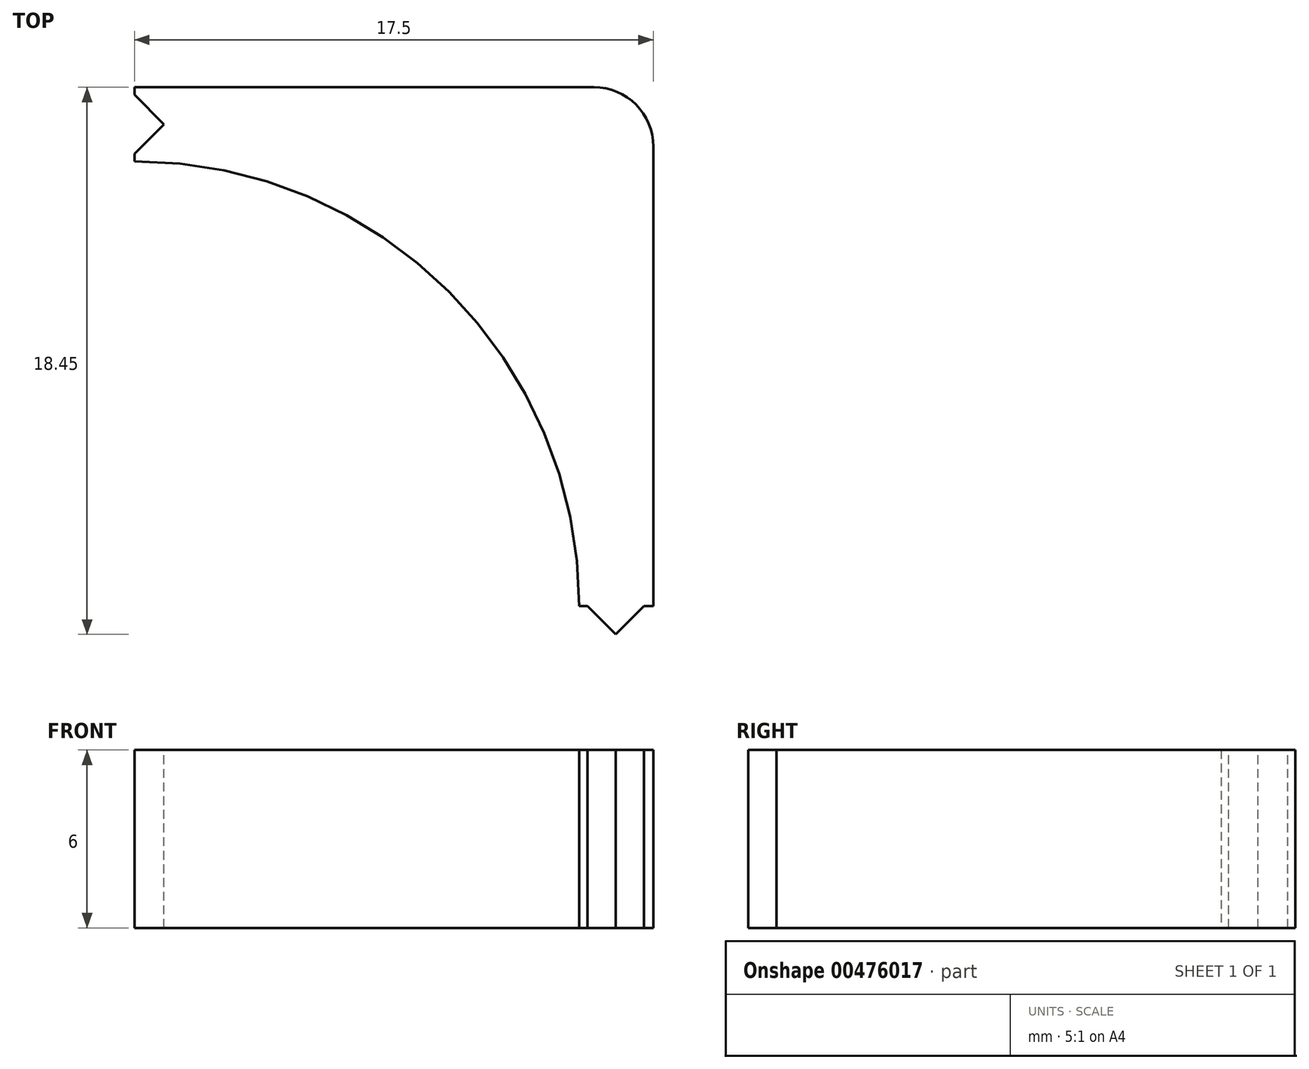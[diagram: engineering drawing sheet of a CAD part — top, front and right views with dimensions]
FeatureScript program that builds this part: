
annotation { "Feature Type Name" : "Feature", "Feature Type Description" : "" }
export const myFeature = defineFeature(function(context is Context, id is Id, definition is map)
    precondition{}
    {
        {
            var Q0;
            Q0=qCreatedBy(makeId("Top.planeOp"),FACE);
            var sketch = newSketch(context, id + "F0", { "sketchPlane" : qUnion([Q0])});
            skLineSegment(sketch, "E0.bottom", {"start": v(-15.5, 17.5) * mm, "end": v(15.5, 17.5) * mm});
            skLineSegment(sketch, "E0.top", {"start": v(-15.5, -17.5) * mm, "end": v(15.5, -17.5) * mm});
            skLineSegment(sketch, "E0.left", {"start": v(-17.5, 15.5) * mm, "end": v(-17.5, -15.5) * mm});
            skLineSegment(sketch, "E0.right", {"start": v(17.5, 15.5) * mm, "end": v(17.5, -15.5) * mm});
            skPoint(sketch, "E0.middle", {"position": v(0, 0) * mm});
            skCircle(sketch, "E1", {"center": v(0, 0) * mm, "radius": 15 * mm});
            skPoint(sketch, "E2.visualSharp", {"position": v(-17.5, 17.5) * mm});
            skArc(sketch, "E2.filletArc", {"start": v(-15.5, 17.5) * mm, "mid": v(-16.91, 16.91) * mm, "end": v(-17.5, 15.5) * mm});
            skPoint(sketch, "E3.visualSharp", {"position": v(17.5, 17.5) * mm});
            skArc(sketch, "E3.filletArc", {"start": v(17.5, 15.5) * mm, "mid": v(16.91, 16.91) * mm, "end": v(15.5, 17.5) * mm});
            skPoint(sketch, "E4.visualSharp", {"position": v(17.5, -17.5) * mm});
            skArc(sketch, "E4.filletArc", {"start": v(15.5, -17.5) * mm, "mid": v(16.91, -16.91) * mm, "end": v(17.5, -15.5) * mm});
            skPoint(sketch, "E5.visualSharp", {"position": v(-17.5, -17.5) * mm});
            skArc(sketch, "E5.filletArc", {"start": v(-17.5, -15.5) * mm, "mid": v(-16.91, -16.91) * mm, "end": v(-15.5, -17.5) * mm});
            skSolve(sketch);
        }
        {
            var Q0;
            Q0 = qSketchRegion(id + "F0", true);
            extrude(context, id + "F1", {"entities" : qUnion([Q0]), "depth" : 6 * mm});
        }
        {
            var Q0;
            Q0=makeQuery(id+"F1.opExtrude","CAP_FACE",FACE,{"disambiguationData":[OSD([sQuery(id+"F0.wireOp",EDGE,"E0.bottom"),sQuery(id+"F0.wireOp",EDGE,"E0.top"),sQuery(id+"F0.wireOp",EDGE,"E0.left"),sQuery(id+"F0.wireOp",EDGE,"E0.right"),sQuery(id+"F0.wireOp",EDGE,"E1"),sQuery(id+"F0.wireOp",EDGE,"E2.filletArc"),sQuery(id+"F0.wireOp",EDGE,"E3.filletArc"),sQuery(id+"F0.wireOp",EDGE,"E4.filletArc"),sQuery(id+"F0.wireOp",EDGE,"E5.filletArc")])],"isStart":false});
            var sketch = newSketch(context, id + "F2", { "sketchPlane" : qUnion([Q0])});
            skLineSegment(sketch, "E6", {"start": v(0, 17.5) * mm, "end": v(0, 0) * mm});
            skLineSegment(sketch, "E7", {"start": v(0, 0) * mm, "end": v(17.5, 0) * mm});
            skLineSegment(sketch, "E8", {"start": v(17.5, 0) * mm, "end": v(17.5, -17.5) * mm});
            skPoint(sketch, "E9.endSnap0", {"position": v(-16.91, -16.91) * mm});
            skLineSegment(sketch, "E10", {"start": v(17.5, -17.5) * mm, "end": v(-17.5, -17.5) * mm});
            skLineSegment(sketch, "E11", {"start": v(-17.5, -17.5) * mm, "end": v(-17.5, 17.5) * mm});
            skLineSegment(sketch, "E12", {"start": v(-17.5, 17.5) * mm, "end": v(0, 17.5) * mm});
            skSolve(sketch);
        }
        {
            var Q0;
            Q0 = qSketchRegion(id + "F2", true);
            extrude(context, id + "F3", {"entities" : qUnion([Q0]), "operationType" : NewBodyOperationType.REMOVE, "oppositeDirection" : true, "depth" : 25 * mm});
        }
        {
            var Q0;
            Q0=makeQuery(id+"F1.opExtrude","CAP_FACE",FACE,{"disambiguationData":[OSD([sQuery(id+"F0.wireOp",EDGE,"E0.bottom"),sQuery(id+"F0.wireOp",EDGE,"E0.top"),sQuery(id+"F0.wireOp",EDGE,"E0.left"),sQuery(id+"F0.wireOp",EDGE,"E0.right"),sQuery(id+"F0.wireOp",EDGE,"E1"),sQuery(id+"F0.wireOp",EDGE,"E2.filletArc"),sQuery(id+"F0.wireOp",EDGE,"E3.filletArc"),sQuery(id+"F0.wireOp",EDGE,"E4.filletArc"),sQuery(id+"F0.wireOp",EDGE,"E5.filletArc")])],"isStart":false});
            var sketch = newSketch(context, id + "F4", { "sketchPlane" : qUnion([Q0])});
            skLineSegment(sketch, "E13", {"start": v(16.25, 0) * mm, "end": v(16.25, -1) * mm, "construction": true});
            skSolve(sketch);
        }
        {
            var Q0;
            Q0=makeQuery(id+"F4.imprint","IMPRINT",FACE,{"disambiguationData":[TD([[makeQuery(id+"F4.imprint","IMPRINT",EDGE,{"derivedFrom":makeQuery(id+"F1.opExtrude","CAP_EDGE",EDGE,{"disambiguationData":[OSD([sQuery(id+"F0.wireOp",EDGE,"E3.filletArc")])],"isStart":false})}),1.0]])]});
            var sketch = newSketch(context, id + "F5", { "sketchPlane" : qUnion([Q0])});
            skLineSegment(sketch, "E14", {"start": v(16.23, -0.95) * mm, "end": v(17.18, 0) * mm});
            skLineSegment(sketch, "E15", {"start": v(17.18, 0) * mm, "end": v(15.28, 0) * mm});
            skLineSegment(sketch, "E16", {"start": v(15.28, 0) * mm, "end": v(16.23, -0.95) * mm});
            skSolve(sketch);
        }
        {
            var Q0;
            Q0 = qSketchRegion(id + "F5", true);
            extrude(context, id + "F6", {"entities" : qUnion([Q0]), "operationType" : NewBodyOperationType.ADD, "oppositeDirection" : true, "depth" : 6 * mm});
        }
        {
            var Q0;
            Q0=makeQuery(id+"F4.imprint","IMPRINT",FACE,{"disambiguationData":[TD([[makeQuery(id+"F4.imprint","IMPRINT",EDGE,{"derivedFrom":makeQuery(id+"F1.opExtrude","CAP_EDGE",EDGE,{"disambiguationData":[OSD([sQuery(id+"F0.wireOp",EDGE,"E3.filletArc")])],"isStart":false})}),1.0]])]});
            var sketch = newSketch(context, id + "F7", { "sketchPlane" : qUnion([Q0])});
            skLineSegment(sketch, "E17", {"start": v(0, 16.25) * mm, "end": v(1, 16.25) * mm, "construction": true});
            skSolve(sketch);
        }
        {
            var Q0;
            Q0=makeQuery(id+"F4.imprint","IMPRINT",FACE,{"disambiguationData":[TD([[makeQuery(id+"F4.imprint","IMPRINT",EDGE,{"derivedFrom":makeQuery(id+"F1.opExtrude","CAP_EDGE",EDGE,{"disambiguationData":[OSD([sQuery(id+"F0.wireOp",EDGE,"E3.filletArc")])],"isStart":false})}),1.0]])]});
            var sketch = newSketch(context, id + "F8", { "sketchPlane" : qUnion([Q0])});
            skLineSegment(sketch, "E18", {"start": v(1, 16.25) * mm, "end": v(0, 17.25) * mm});
            skLineSegment(sketch, "E19", {"start": v(0, 17.25) * mm, "end": v(0, 15.25) * mm});
            skLineSegment(sketch, "E20", {"start": v(0, 15.25) * mm, "end": v(1, 16.25) * mm});
            skSolve(sketch);
        }
        {
            var Q0;
            Q0 = qSketchRegion(id + "F8", true);
            extrude(context, id + "F9", {"entities" : qUnion([Q0]), "operationType" : NewBodyOperationType.REMOVE, "oppositeDirection" : true, "depth" : 6 * mm});
        }
    });
